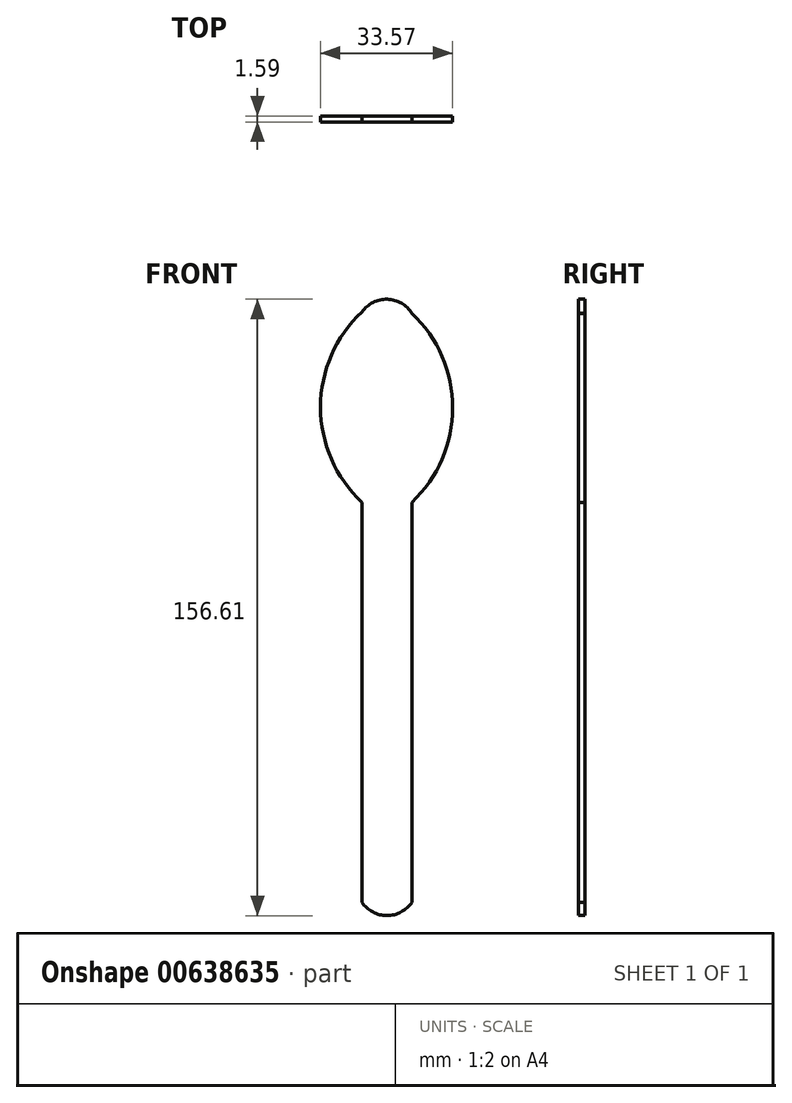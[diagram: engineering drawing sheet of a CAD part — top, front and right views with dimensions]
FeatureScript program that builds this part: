
annotation { "Feature Type Name" : "Feature", "Feature Type Description" : "" }
export const myFeature = defineFeature(function(context is Context, id is Id, definition is map)
    precondition{}
    {
        {
            var Q0;
            Q0=qCreatedBy(makeId("Front.planeOp"),FACE);
            var sketch = newSketch(context, id + "F0", { "sketchPlane" : qUnion([Q0])});
            skLineSegment(sketch, "E0", {"start": v(-6.35, 0) * mm, "end": v(-6.35, -9.53) * mm});
            skLineSegment(sketch, "E1", {"start": v(-6.35, -9.53) * mm, "end": v(6.35, -9.53) * mm});
            skLineSegment(sketch, "E2", {"start": v(6.35, -9.53) * mm, "end": v(6.35, 92.07) * mm});
            skLineSegment(sketch, "E3", {"start": v(6.35, 92.07) * mm, "end": v(-6.35, 92.07) * mm});
            skLineSegment(sketch, "E4", {"start": v(-6.35, 92.07) * mm, "end": v(-6.35, 0) * mm});
            skArc(sketch, "E5", {"start": v(-6.35, -9.53) * mm, "mid": v(0, -12.94) * mm, "end": v(6.35, -9.53) * mm});
            skArc(sketch, "E6", {"start": v(6.35, 140.08) * mm, "mid": v(0.1, 143.67) * mm, "end": v(-6.35, 140.44) * mm});
            skArc(sketch, "E7", {"start": v(-6.35, 140.44) * mm, "mid": v(-16.88, 116.25) * mm, "end": v(-6.35, 92.07) * mm});
            skArc(sketch, "E8", {"start": v(6.35, 92.07) * mm, "mid": v(16.7, 116.07) * mm, "end": v(6.35, 140.08) * mm});
            skSolve(sketch);
        }
        {
            var Q0;
            Q0 = qSketchRegion(id + "F0", true);
            extrude(context, id + "F1", {"entities" : qUnion([Q0]), "depth" : 1.59 * mm, "offsetDistance" : 25.4 * mm});
        }
    });
